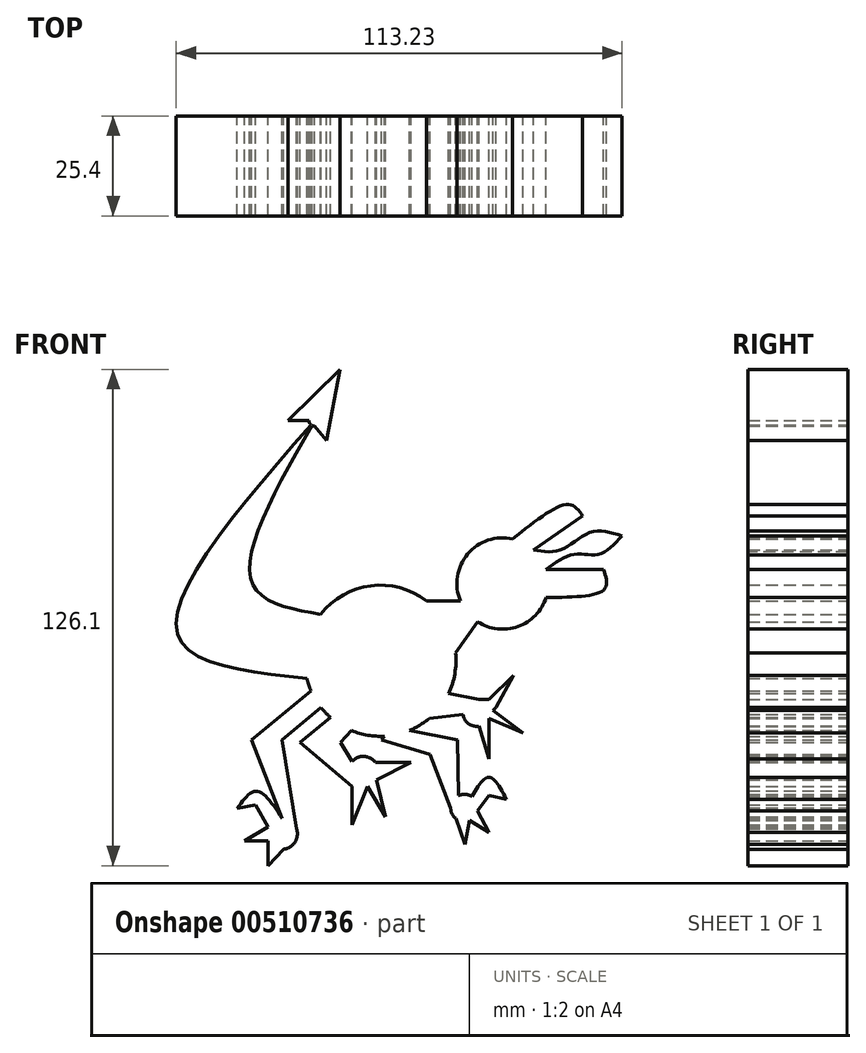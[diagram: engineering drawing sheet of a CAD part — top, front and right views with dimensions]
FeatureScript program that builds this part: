
annotation { "Feature Type Name" : "Feature", "Feature Type Description" : "" }
export const myFeature = defineFeature(function(context is Context, id is Id, definition is map)
    precondition{}
    {
        {
            var Q0;
            Q0=qCreatedBy(makeId("Front.planeOp"),FACE);
            var sketch = newSketch(context, id + "F0", { "sketchPlane" : qUnion([Q0])});
            skCircle(sketch, "E0", {"center": v(-27.6, -6.36) * mm, "radius": 19.2 * mm});
            skCircle(sketch, "E1", {"center": v(3.45, 13.26) * mm, "radius": 11.6 * mm});
            skCircle(sketch, "E2", {"center": v(-52.61, -50.37) * mm, "radius": 3.92 * mm});
            skCircle(sketch, "E3", {"center": v(-6.28, -43.75) * mm, "radius": 3.47 * mm});
            skCircle(sketch, "E4", {"center": v(-44.32, 54.68) * mm, "radius": 1.44 * mm});
            skLineSegment(sketch, "E5", {"start": v(-15.88, 8.85) * mm, "end": v(-7.28, 8.85) * mm});
            skLineSegment(sketch, "E6", {"start": v(-8.5, -4.36) * mm, "end": v(-2.88, 3.54) * mm});
            skCircle(sketch, "E7", {"center": v(-31.94, -34.56) * mm, "radius": 3.9 * mm});
            skCircle(sketch, "E8", {"center": v(-3.17, -19.57) * mm, "radius": 3.45 * mm});
            skLineSegment(sketch, "E9", {"start": v(-34.82, -38.28) * mm, "end": v(-34.82, -48.06) * mm});
            skLineSegment(sketch, "E10", {"start": v(-30.92, -38.31) * mm, "end": v(-34.82, -48.06) * mm});
            skLineSegment(sketch, "E11", {"start": v(-30.92, -38.31) * mm, "end": v(-26.3, -46.06) * mm});
            skLineSegment(sketch, "E12", {"start": v(-28.61, -36.58) * mm, "end": v(-26.3, -46.06) * mm});
            skPoint(sketch, "E12.startSnap0", {"position": v(-28.61, -42.18) * mm});
            skLineSegment(sketch, "E13", {"start": v(-28.88, -32.15) * mm, "end": v(-19.86, -32.15) * mm});
            skLineSegment(sketch, "E14", {"start": v(-28.61, -36.58) * mm, "end": v(-19.86, -32.15) * mm});
            skLineSegment(sketch, "E15", {"start": v(-30.92, -13.24) * mm, "end": v(-48.06, -27.05) * mm});
            skLineSegment(sketch, "E16", {"start": v(-48.06, -27.05) * mm, "end": v(-34.82, -38.28) * mm});
            skLineSegment(sketch, "E17", {"start": v(-28.61, -17.56) * mm, "end": v(-37.7, -27.05) * mm});
            skLineSegment(sketch, "E18", {"start": v(-10.32, -14.71) * mm, "end": v(-2.53, -16.18) * mm});
            skLineSegment(sketch, "E19", {"start": v(-15.2, -21) * mm, "end": v(-6.6, -19.98) * mm});
            skPoint(sketch, "E20.end.orphan", {"position": v(-34.82, -28.76) * mm});
            skLineSegment(sketch, "E21", {"start": v(-37.7, -27.05) * mm, "end": v(-34.82, -31.95) * mm});
            skLineSegment(sketch, "E22", {"start": v(-2.53, -22.96) * mm, "end": v(0, -31.33) * mm});
            skLineSegment(sketch, "E23", {"start": v(0, -31.33) * mm, "end": v(0, -20.95) * mm});
            skLineSegment(sketch, "E24", {"start": v(0, -20.95) * mm, "end": v(8.63, -24.75) * mm});
            skLineSegment(sketch, "E25", {"start": v(8.63, -24.75) * mm, "end": v(0, -18.2) * mm});
            skLineSegment(sketch, "E26", {"start": v(-52.6, -46.45) * mm, "end": v(-60.38, -26.48) * mm});
            skLineSegment(sketch, "E27", {"start": v(-60.38, -26.48) * mm, "end": v(-45.23, -13.97) * mm});
            skLineSegment(sketch, "E28", {"start": v(-48.7, -50.37) * mm, "end": v(-52.6, -26.48) * mm});
            skLineSegment(sketch, "E29", {"start": v(-52.6, -26.48) * mm, "end": v(-42.66, -18.27) * mm});
            skLineSegment(sketch, "E30", {"start": v(-7.78, -40.62) * mm, "end": v(-8.04, -26.48) * mm});
            skLineSegment(sketch, "E31", {"start": v(-8.04, -26.48) * mm, "end": v(-20.27, -24.1) * mm});
            skLineSegment(sketch, "E32", {"start": v(-9.74, -43.75) * mm, "end": v(-15.03, -30.18) * mm});
            skLineSegment(sketch, "E33", {"start": v(-15.03, -30.18) * mm, "end": v(-27.36, -26.48) * mm});
            skLineSegment(sketch, "E34", {"start": v(-52.19, -54.26) * mm, "end": v(-56.12, -58.42) * mm});
            skLineSegment(sketch, "E35", {"start": v(-56.12, -58.42) * mm, "end": v(-56.12, -52.1) * mm});
            skLineSegment(sketch, "E36", {"start": v(-56.12, -52.1) * mm, "end": v(-62.17, -52.1) * mm});
            skLineSegment(sketch, "E37", {"start": v(-62.17, -52.1) * mm, "end": v(-56.12, -48.63) * mm});
            skPoint(sketch, "E38.start.orphan", {"position": v(0, -16.18) * mm});
            skPoint(sketch, "E39.end.orphan", {"position": v(1.78, -18.2) * mm});
            skFitSpline(sketch, "E40", {"points": [v(-42.78, 5.4) * mm, v(-60.2, 13.36) * mm, v(-44.32, 54.68) * mm], "startDerivative": vector(-57.68, 10.38) * mm, "endDerivative": vector(47.44, 83.08) * mm});
            skFitSpline(sketch, "E41", {"points": [v(-46.28, -10.8) * mm, v(-78.98, 0) * mm, v(-44.32, 54.68) * mm], "startDerivative": vector(-106.44, 11.09) * mm, "endDerivative": vector(99.66, 114.48) * mm});
            skLineSegment(sketch, "E42", {"start": v(-44.32, 54.68) * mm, "end": v(-51.09, 54.68) * mm});
            skLineSegment(sketch, "E43", {"start": v(-44.32, 53.24) * mm, "end": v(-41.31, 49.57) * mm});
            skLineSegment(sketch, "E44", {"start": v(-41.31, 49.57) * mm, "end": v(-37.88, 67.68) * mm});
            skLineSegment(sketch, "E45", {"start": v(-37.88, 67.68) * mm, "end": v(-51.09, 54.68) * mm});
            skFitSpline(sketch, "E46", {"points": [v(-52.6, -46.45) * mm, v(-59.02, -39.5) * mm, v(-64, -43.9) * mm], "startDerivative": vector(-12.04, 18.9) * mm, "endDerivative": vector(-10.75, -14.78) * mm});
            skFitSpline(sketch, "E47", {"points": [v(-56.12, -48.63) * mm, v(-59.31, -43.02) * mm], "startDerivative": vector(-3.19, 5.6) * mm, "endDerivative": vector(-3.19, 5.6) * mm});
            skLineSegment(sketch, "E48", {"start": v(-8.44, -46.45) * mm, "end": v(-6.17, -53) * mm});
            skLineSegment(sketch, "E49", {"start": v(-4.97, -46.95) * mm, "end": v(-6.17, -53) * mm});
            skLineSegment(sketch, "E50", {"start": v(-4.97, -46.95) * mm, "end": v(0, -49.98) * mm});
            skPoint(sketch, "E50.endSnap0", {"position": v(-5.57, -49.98) * mm});
            skLineSegment(sketch, "E51", {"start": v(-2.88, -44.45) * mm, "end": v(0, -49.98) * mm});
            skLineSegment(sketch, "E52", {"start": v(-59.31, -43.02) * mm, "end": v(-64, -43.9) * mm});
            skLineSegment(sketch, "E53", {"start": v(-27.36, -26.48) * mm, "end": v(-24.37, -22.94) * mm});
            skPoint(sketch, "E53.endSnap0", {"position": v(-24.37, -32.15) * mm});
            skFitSpline(sketch, "E54", {"points": [v(-4.36, -40.86) * mm, v(0, -35.97) * mm, v(4.4, -41.55) * mm], "startDerivative": vector(8.96, 15.07) * mm, "endDerivative": vector(8.56, -16.26) * mm});
            skFitSpline(sketch, "E55", {"points": [v(-2.88, -44.45) * mm, v(0, -40.62) * mm], "startDerivative": vector(2.88, 3.83) * mm, "endDerivative": vector(2.88, 3.83) * mm});
            skLineSegment(sketch, "E56", {"start": v(4.4, -41.55) * mm, "end": v(0, -40.62) * mm});
            skLineSegment(sketch, "E57", {"start": v(0, -16.18) * mm, "end": v(-2.53, -16.18) * mm});
            skLineSegment(sketch, "E58", {"start": v(1.78, -18.2) * mm, "end": v(0, -18.2) * mm});
            skLineSegment(sketch, "E59", {"start": v(0, -16.18) * mm, "end": v(-1.1, -16.8) * mm});
            skLineSegment(sketch, "E60", {"start": v(1.78, -18.2) * mm, "end": v(0.28, -19.86) * mm});
            skLineSegment(sketch, "E61", {"start": v(0, -16.18) * mm, "end": v(6.17, -10.13) * mm});
            skLineSegment(sketch, "E62", {"start": v(1.78, -18.2) * mm, "end": v(6.17, -10.13) * mm});
            skLineSegment(sketch, "E63", {"start": v(0, -16.18) * mm, "end": v(-0.81, -17.05) * mm});
            skPoint(sketch, "E64.start.orphan", {"position": v(0, 24.34) * mm});
            skFitSpline(sketch, "E65", {"points": [v(6, 24.58) * mm, v(20.26, 33.33) * mm, v(23.78, 30.39) * mm], "startDerivative": vector(25.48, 20.45) * mm, "endDerivative": vector(8.28, -12.3) * mm});
            skLineSegment(sketch, "E66", {"start": v(23.78, 30.39) * mm, "end": v(11.3, 21.81) * mm});
            skFitSpline(sketch, "E67", {"points": [v(14.5, 9.74) * mm, v(29.36, 11.9) * mm, v(29.07, 16.88) * mm], "startDerivative": vector(31.08, 0.17) * mm, "endDerivative": vector(-5.23, 15.5) * mm});
            skLineSegment(sketch, "E68", {"start": v(29.07, 16.88) * mm, "end": v(14.47, 16.88) * mm});
            skPoint(sketch, "E69.endSnap0", {"position": v(21.77, 16.88) * mm});
            skPoint(sketch, "E70.end.orphan", {"position": v(25.84, 20.7) * mm});
            skPoint(sketch, "E71.end.orphan", {"position": v(18.19, 16.88) * mm});
            skPoint(sketch, "E72.end.orphan", {"position": v(21.77, 20.7) * mm});
            skPoint(sketch, "E69.end.orphan", {"position": v(25.84, 16.88) * mm});
            skFitSpline(sketch, "E73", {"points": [v(11.3, 21.81) * mm, v(18.2, 21.81) * mm, v(25.84, 26.28) * mm, v(33.77, 25.4) * mm], "startDerivative": vector(22.42, -4.17) * mm, "endDerivative": vector(24.22, -7.5) * mm});
            skFitSpline(sketch, "E74", {"points": [v(14.47, 16.88) * mm, v(21.77, 20.7) * mm, v(27.9, 20.7) * mm, v(33.77, 25.4) * mm], "startDerivative": vector(20.54, 14.74) * mm, "endDerivative": vector(16.6, 18.4) * mm});
            skSolve(sketch);
        }
        {
            var Q0;
            Q0 = qSketchRegion(id + "F0", true);
            extrude(context, id + "F1", {"entities" : qUnion([Q0]), "depth" : 25.4 * mm, "offsetDistance" : 25.4 * mm});
        }
        {
            var Q0;
            Q0 = qSketchRegion(id + "F0", true);
            extrude(context, id + "F2", {"entities" : qUnion([Q0]), "operationType" : NewBodyOperationType.ADD, "depth" : 25.4 * mm, "offsetDistance" : 25.4 * mm});
        }
    });
